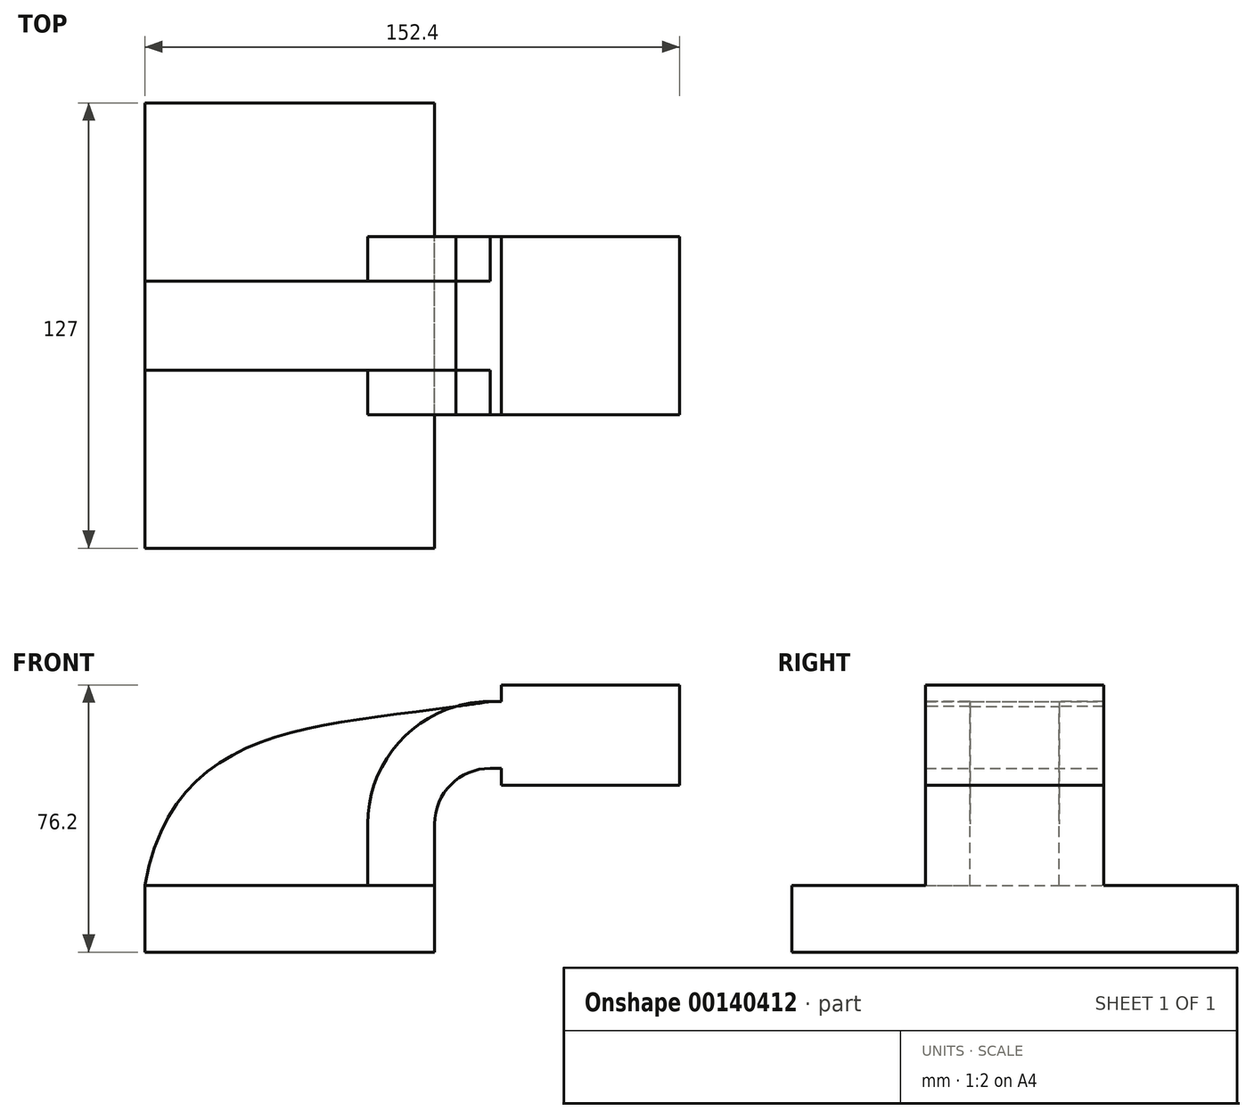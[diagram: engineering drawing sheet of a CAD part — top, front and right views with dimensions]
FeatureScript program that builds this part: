
annotation { "Feature Type Name" : "Feature", "Feature Type Description" : "" }
export const myFeature = defineFeature(function(context is Context, id is Id, definition is map)
    precondition{}
    {
        {
            var Q0;
            Q0=qCreatedBy(makeId("Front.planeOp"),FACE);
            var sketch = newSketch(context, id + "F0", { "sketchPlane" : qUnion([Q0])});
            skLineSegment(sketch, "E0.bottom", {"start": v(41.28, 9.53) * mm, "end": v(-41.28, 9.52) * mm});
            skLineSegment(sketch, "E0.top", {"start": v(41.28, -9.52) * mm, "end": v(-41.28, -9.53) * mm});
            skLineSegment(sketch, "E0.left", {"start": v(41.28, 9.53) * mm, "end": v(41.28, -9.52) * mm});
            skLineSegment(sketch, "E0.right", {"start": v(-41.28, 9.52) * mm, "end": v(-41.28, -9.53) * mm});
            skPoint(sketch, "E0.middle", {"position": v(0, 0) * mm});
            skLineSegment(sketch, "E1.bottom", {"start": v(111.12, 66.68) * mm, "end": v(60.32, 66.68) * mm});
            skLineSegment(sketch, "E1.top", {"start": v(111.12, 38.1) * mm, "end": v(60.32, 38.1) * mm});
            skLineSegment(sketch, "E1.left", {"start": v(111.12, 66.68) * mm, "end": v(111.12, 38.1) * mm});
            skLineSegment(sketch, "E1.right", {"start": v(60.32, 66.68) * mm, "end": v(60.32, 38.1) * mm});
            skPoint(sketch, "E1.middle", {"position": v(85.72, 52.39) * mm});
            skLineSegment(sketch, "E2", {"start": v(41.28, 9.53) * mm, "end": v(41.27, 27) * mm});
            skArc(sketch, "E3", {"start": v(41.28, 27) * mm, "mid": v(45.92, 38.23) * mm, "end": v(57.15, 42.88) * mm});
            skLineSegment(sketch, "E4", {"start": v(57.15, 42.88) * mm, "end": v(85.76, 42.88) * mm});
            skLineSegment(sketch, "E5.0", {"start": v(57.15, 61.93) * mm, "end": v(85.76, 61.93) * mm});
            skArc(sketch, "E5.1", {"start": v(22.23, 27) * mm, "mid": v(32.45, 51.7) * mm, "end": v(57.15, 61.93) * mm});
            skLineSegment(sketch, "E5.2", {"start": v(22.23, 9.53) * mm, "end": v(22.23, 27) * mm});
            skFitSpline(sketch, "E6", {"points": [v(-41.28, 9.52) * mm, v(57.15, 61.93) * mm], "startDerivative": vector(25.34, 142.46) * mm, "endDerivative": vector(145.16, 22.3) * mm});
            skSolve(sketch);
        }
        {
            var Q0;
            Q0=makeQuery(id+"F0.imprint","IMPRINT",FACE,{"disambiguationData":[TD([[makeQuery(id+"F0.imprint","IMPRINT",EDGE,{"derivedFrom":sQuery(id+"F0.wireOp",EDGE,"E0.top")}),-1.0]])]});
            extrude(context, id + "F1", {"entities" : qUnion([Q0]), "endBound" : BoundingType.SYMMETRIC, "depth" : 127 * mm});
        }
        {
            var Q0;
            {var subQ1=sQuery(id+"F0.wireOp",EDGE,"E2");Q0=makeQuery(id+"F0.imprint","IMPRINT",FACE,{"disambiguationData":[TD([[makeQuery(id+"F0.imprint","IMPRINT",EDGE,{"derivedFrom":subQ1}),1.0]])]});}
            var Q1;
            {var subQ1=sQuery(id+"F0.wireOp",EDGE,"E1.bottom");Q1=makeQuery(id+"F0.imprint","IMPRINT",FACE,{"disambiguationData":[TD([[makeQuery(id+"F0.imprint","IMPRINT",EDGE,{"derivedFrom":subQ1}),1.0]])]});}
            extrude(context, id + "F2", {"entities" : qUnion([Q0, Q1]), "operationType" : NewBodyOperationType.ADD, "endBound" : BoundingType.SYMMETRIC, "depth" : 50.8 * mm});
        }
        {
            var Q0;
            Q0 = qSketchRegion(id + "F0", true);
            extrude(context, id + "F3", {"entities" : qUnion([Q0]), "operationType" : NewBodyOperationType.ADD, "endBound" : BoundingType.SYMMETRIC, "depth" : 25.4 * mm});
        }
    });
